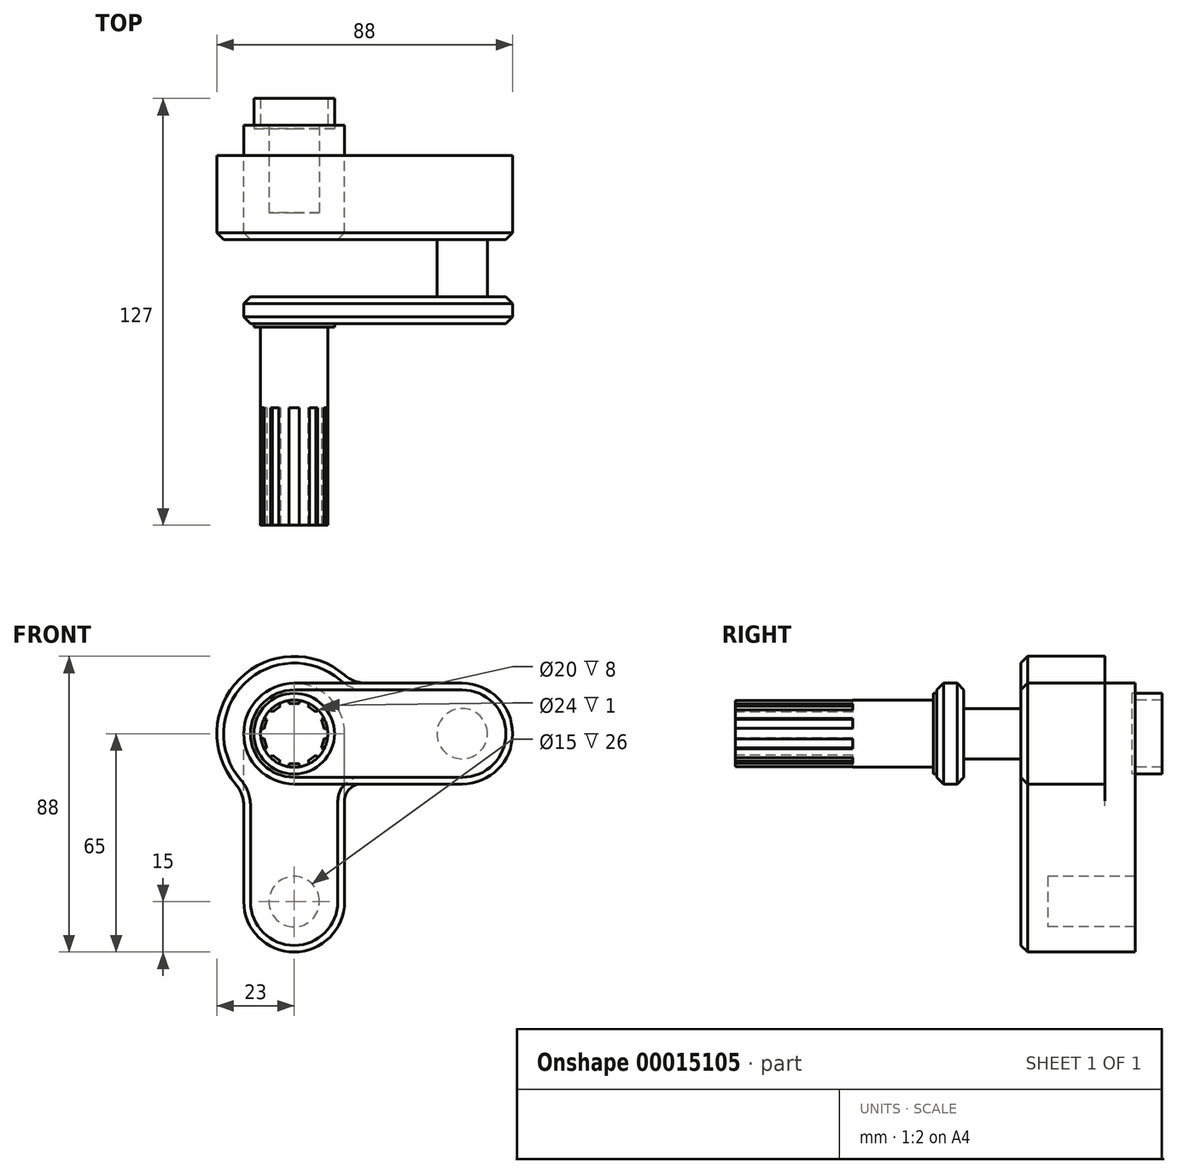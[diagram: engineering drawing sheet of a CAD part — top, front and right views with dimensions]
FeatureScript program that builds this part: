
annotation { "Feature Type Name" : "Feature", "Feature Type Description" : "" }
export const myFeature = defineFeature(function(context is Context, id is Id, definition is map)
    precondition{}
    {
        {
            var Q0;
            Q0=qCreatedBy(makeId("Front.planeOp"),FACE);
            var sketch = newSketch(context, id + "F0", { "sketchPlane" : qUnion([Q0])});
            skArc(sketch, "E0", {"start": v(15.01, 17.42) * mm, "mid": v(-16.26, 16.26) * mm, "end": v(-17.42, -15.01) * mm});
            skLineSegment(sketch, "E1", {"start": v(0, 0) * mm, "end": v(77.35, 0) * mm, "construction": true});
            skLineSegment(sketch, "E2", {"start": v(0, 0) * mm, "end": v(0, -78.85) * mm, "construction": true});
            skArc(sketch, "E3", {"start": v(50, -15) * mm, "mid": v(65, 0) * mm, "end": v(50, 15) * mm});
            skArc(sketch, "E4", {"start": v(-15, -50) * mm, "mid": v(0, -65) * mm, "end": v(15, -50) * mm});
            skLineSegment(sketch, "E5", {"start": v(50, 15) * mm, "end": v(0, 15) * mm});
            skLineSegment(sketch, "E6", {"start": v(50, -15) * mm, "end": v(0, -15) * mm});
            skLineSegment(sketch, "E7", {"start": v(-15, -50) * mm, "end": v(-15, 0) * mm});
            skLineSegment(sketch, "E8", {"start": v(15, -50) * mm, "end": v(15, 0) * mm});
            skPoint(sketch, "E9.visualSharp", {"position": v(15, -15) * mm});
            skArc(sketch, "E9.filletArc", {"start": v(20, -15) * mm, "mid": v(16.46, -16.46) * mm, "end": v(15, -20) * mm});
            skPoint(sketch, "E10.visualSharp", {"position": v(-15, -17.44) * mm});
            skArc(sketch, "E10.filletArc", {"start": v(-15, -21.54) * mm, "mid": v(-15.63, -18.06) * mm, "end": v(-17.42, -15.01) * mm});
            skPoint(sketch, "E11.visualSharp", {"position": v(17.44, 15) * mm});
            skArc(sketch, "E11.filletArc", {"start": v(15.01, 17.42) * mm, "mid": v(18.06, 15.63) * mm, "end": v(21.54, 15) * mm});
            skCircle(sketch, "E12", {"center": v(0, 0) * mm, "radius": 10 * mm});
            skCircle(sketch, "E13", {"center": v(0, 0) * mm, "radius": 12 * mm});
            skCircle(sketch, "E14", {"center": v(50, 0) * mm, "radius": 7.5 * mm});
            skCircle(sketch, "E15", {"center": v(0, -50) * mm, "radius": 7.5 * mm});
            skCircle(sketch, "E16", {"center": v(0, 0) * mm, "radius": 15 * mm});
            skSolve(sketch);
        }
        {
            var Q0;
            Q0=makeQuery(id+"F0.imprint","IMPRINT",FACE,{"disambiguationData":[TD([[makeQuery(id+"F0.imprint","IMPRINT",EDGE,{"derivedFrom":sQuery(id+"F0.wireOp",EDGE,"E0")}),1.0]])]});
            var Q1;
            {var subQ4=sQuery(id+"F0.wireOp",EDGE,"E4");Q1=makeQuery(id+"F0.imprint","IMPRINT",FACE,{"disambiguationData":[TD([[makeQuery(id+"F0.imprint","IMPRINT",EDGE,{"derivedFrom":subQ4}),1.0]])]});}
            var Q2;
            {var subQ0=sQuery(id+"F0.wireOp",EDGE,"E9.filletArc");Q2=makeQuery(id+"F0.imprint","IMPRINT",FACE,{"disambiguationData":[TD([[makeQuery(id+"F0.imprint","IMPRINT",EDGE,{"derivedFrom":subQ0}),-1.0]])]});}
            var Q3;
            {var subQ8=sQuery(id+"F0.wireOp",EDGE,"E3");Q3=makeQuery(id+"F0.imprint","IMPRINT",FACE,{"disambiguationData":[TD([[makeQuery(id+"F0.imprint","IMPRINT",EDGE,{"derivedFrom":subQ8}),1.0]])]});}
            var Q4;
            Q4=makeQuery(id+"F0.imprint","IMPRINT",FACE,{"disambiguationData":[TD([[makeQuery(id+"F0.imprint","IMPRINT",EDGE,{"derivedFrom":sQuery(id+"F0.wireOp",EDGE,"E13")}),-1.0]])]});
            var Q5;
            Q5=makeQuery(id+"F0.imprint","IMPRINT",FACE,{"disambiguationData":[TD([[makeQuery(id+"F0.imprint","IMPRINT",EDGE,{"derivedFrom":sQuery(id+"F0.wireOp",EDGE,"E12")}),-1.0]])]});
            var Q6;
            Q6=makeQuery(id+"F0.imprint","IMPRINT",FACE,{"disambiguationData":[TD([[makeQuery(id+"F0.imprint","IMPRINT",EDGE,{"derivedFrom":sQuery(id+"F0.wireOp",EDGE,"E12")}),1.0]])]});
            var Q7;
            {var subQ0=sQuery(id+"F0.wireOp",EDGE,"E16");var subQ3=sQuery(id+"F0.wireOp",EDGE,"E6");var subQ4=makeQuery(id+"F0.imprint","INTERSECT",VERTEX,{"derivedFrom":[subQ3,subQ0]});Q7=makeQuery(id+"F0.imprint","IMPRINT",FACE,{"disambiguationData":[TD([[makeQuery(id+"F0.imprint","IMPRINT",EDGE,{"disambiguationData":[TD([[subQ4,1.0]])],"derivedFrom":subQ3}),-1.0]])]});}
            var Q8;
            Q8=makeQuery(id+"F0.imprint","IMPRINT",FACE,{"disambiguationData":[TD([[makeQuery(id+"F0.imprint","IMPRINT",EDGE,{"derivedFrom":sQuery(id+"F0.wireOp",EDGE,"E14")}),1.0]])]});
            var Q9;
            Q9=makeQuery(id+"F0.imprint","IMPRINT",FACE,{"disambiguationData":[TD([[makeQuery(id+"F0.imprint","IMPRINT",EDGE,{"derivedFrom":sQuery(id+"F0.wireOp",EDGE,"E15")}),1.0]])]});
            extrude(context, id + "F1", {"entities" : qUnion([Q0, Q1, Q2, Q3, Q4, Q5, Q6, Q7, Q8, Q9]), "endBound" : BoundingType.SYMMETRIC, "depth" : 8 * mm});
        }
        {
            var Q0;
            Q0=makeQuery(id+"F1.opExtrude","CAP_FACE",FACE,{"disambiguationData":[OSD([sQuery(id+"F0.wireOp",EDGE,"E0"),sQuery(id+"F0.wireOp",EDGE,"E3"),sQuery(id+"F0.wireOp",EDGE,"E4"),sQuery(id+"F0.wireOp",EDGE,"E5"),sQuery(id+"F0.wireOp",EDGE,"E6"),sQuery(id+"F0.wireOp",EDGE,"E7"),sQuery(id+"F0.wireOp",EDGE,"E8"),sQuery(id+"F0.wireOp",EDGE,"E9.filletArc"),sQuery(id+"F0.wireOp",EDGE,"E10.filletArc"),sQuery(id+"F0.wireOp",EDGE,"E11.filletArc")])],"isStart":false});
            var sketch = newSketch(context, id + "F2", { "sketchPlane" : qUnion([Q0])});
            skCircle(sketch, "E17.0", {"center": v(50, 0) * mm, "radius": 7.5 * mm});
            skSolve(sketch);
        }
        {
            var Q0;
            Q0=makeQuery(id+"F2.imprint","IMPRINT",FACE,{"disambiguationData":[TD([[makeQuery(id+"F2.imprint","IMPRINT",EDGE,{"derivedFrom":sQuery(id+"F2.wireOp",EDGE,"E17.0")}),1.0]])]});
            extrude(context, id + "F3", {"entities" : qUnion([Q0]), "operationType" : NewBodyOperationType.ADD, "depth" : 17 * mm});
        }
        {
            var Q0;
            Q0=makeQuery(id+"F3.opExtrude","CAP_FACE",FACE,{"disambiguationData":[OSD([sQuery(id+"F2.wireOp",EDGE,"E17.0")])],"isStart":false});
            var sketch = newSketch(context, id + "F4", { "sketchPlane" : qUnion([Q0])});
            skArc(sketch, "E18.0", {"start": v(50, -15) * mm, "mid": v(65, 0) * mm, "end": v(50, 15) * mm});
            skLineSegment(sketch, "E18.1", {"start": v(50, 15) * mm, "end": v(0, 15) * mm});
            skLineSegment(sketch, "E18.2", {"start": v(50, -15) * mm, "end": v(0, -15) * mm});
            skArc(sketch, "E18.3", {"start": v(0, 15) * mm, "mid": v(-15, 0) * mm, "end": v(0, -15) * mm});
            skSolve(sketch);
        }
        {
            var Q0;
            Q0=makeQuery(id+"F4.imprint","IMPRINT",FACE,{"disambiguationData":[TD([[makeQuery(id+"F4.imprint","IMPRINT",EDGE,{"derivedFrom":sQuery(id+"F4.wireOp",EDGE,"E18.0")}),1.0]])]});
            var Q1;
            Q1=makeQuery(id+"F4.imprint","IMPRINT",FACE,{"disambiguationData":[TD([[makeQuery(id+"F4.imprint","IMPRINT",EDGE,{"derivedFrom":makeQuery(id+"F3.opExtrude","CAP_EDGE",EDGE,{"disambiguationData":[OSD([sQuery(id+"F2.wireOp",EDGE,"E17.0")])],"isStart":false})}),1.0]])]});
            extrude(context, id + "F5", {"entities" : qUnion([Q0, Q1]), "operationType" : NewBodyOperationType.ADD, "depth" : 8 * mm});
        }
        {
            var Q0;
            Q0=makeQuery(id+"F5.opExtrude","CAP_FACE",FACE,{"disambiguationData":[OSD([sQuery(id+"F4.wireOp",EDGE,"E18.0"),sQuery(id+"F4.wireOp",EDGE,"E18.1"),sQuery(id+"F4.wireOp",EDGE,"E18.2"),sQuery(id+"F4.wireOp",EDGE,"E18.3")])],"isStart":false});
            var sketch = newSketch(context, id + "F6", { "sketchPlane" : qUnion([Q0])});
            skCircle(sketch, "E19.0", {"center": v(0, 0) * mm, "radius": 12 * mm});
            skSolve(sketch);
        }
        {
            var Q0;
            Q0=makeQuery(id+"F6.imprint","IMPRINT",FACE,{"disambiguationData":[TD([[makeQuery(id+"F6.imprint","IMPRINT",EDGE,{"derivedFrom":sQuery(id+"F6.wireOp",EDGE,"E19.0")}),1.0]])]});
            extrude(context, id + "F7", {"entities" : qUnion([Q0]), "operationType" : NewBodyOperationType.ADD, "depth" : 1 * mm});
        }
        {
            var Q0;
            Q0=makeQuery(id+"F7.opExtrude","CAP_FACE",FACE,{"disambiguationData":[OSD([sQuery(id+"F6.wireOp",EDGE,"E19.0")])],"isStart":false});
            var sketch = newSketch(context, id + "F8", { "sketchPlane" : qUnion([Q0])});
            skCircle(sketch, "E20.0", {"center": v(0, 0) * mm, "radius": 10 * mm});
            skSolve(sketch);
        }
        {
            var Q0;
            Q0=makeQuery(id+"F8.imprint","IMPRINT",FACE,{"disambiguationData":[TD([[makeQuery(id+"F8.imprint","IMPRINT",EDGE,{"derivedFrom":sQuery(id+"F8.wireOp",EDGE,"E20.0")}),1.0]])]});
            extrude(context, id + "F9", {"entities" : qUnion([Q0]), "operationType" : NewBodyOperationType.ADD, "depth" : 59 * mm});
        }
        {
            var Q0;
            Q0=makeQuery(id+"F1.opExtrude","CAP_FACE",FACE,{"disambiguationData":[OSD([sQuery(id+"F0.wireOp",EDGE,"E0"),sQuery(id+"F0.wireOp",EDGE,"E3"),sQuery(id+"F0.wireOp",EDGE,"E4"),sQuery(id+"F0.wireOp",EDGE,"E5"),sQuery(id+"F0.wireOp",EDGE,"E6"),sQuery(id+"F0.wireOp",EDGE,"E7"),sQuery(id+"F0.wireOp",EDGE,"E8"),sQuery(id+"F0.wireOp",EDGE,"E9.filletArc"),sQuery(id+"F0.wireOp",EDGE,"E10.filletArc"),sQuery(id+"F0.wireOp",EDGE,"E11.filletArc")])],"isStart":true});
            var sketch = newSketch(context, id + "F10", { "sketchPlane" : qUnion([Q0])});
            skCircle(sketch, "E21.0", {"center": v(0, -50) * mm, "radius": 7.5 * mm});
            skSolve(sketch);
        }
        {
            var Q0;
            Q0=makeQuery(id+"F10.imprint","IMPRINT",FACE,{"disambiguationData":[TD([[makeQuery(id+"F10.imprint","IMPRINT",EDGE,{"derivedFrom":sQuery(id+"F10.wireOp",EDGE,"E21.0")}),-1.0]])]});
            extrude(context, id + "F11", {"entities" : qUnion([Q0]), "operationType" : NewBodyOperationType.ADD, "depth" : 17 * mm});
        }
        {
            var Q0;
            Q0=makeQuery(id+"F11.opExtrude","CAP_FACE",FACE,{"disambiguationData":[OSD([sQuery(id+"F10.wireOp",EDGE,"E21.0")])],"isStart":false});
            var sketch = newSketch(context, id + "F12", { "sketchPlane" : qUnion([Q0])});
            skArc(sketch, "E22.0", {"start": v(15, -50) * mm, "mid": v(0, -65) * mm, "end": v(-15, -50) * mm});
            skLineSegment(sketch, "E23.0", {"start": v(-15, -50) * mm, "end": v(-15, 0) * mm});
            skLineSegment(sketch, "E24.0", {"start": v(15, -50) * mm, "end": v(15, 0) * mm});
            skArc(sketch, "E25.0", {"start": v(-15, 0) * mm, "mid": v(0, 15) * mm, "end": v(15, 0) * mm});
            skSolve(sketch);
        }
        {
            var Q0;
            Q0=makeQuery(id+"F12.imprint","IMPRINT",FACE,{"disambiguationData":[TD([[makeQuery(id+"F12.imprint","IMPRINT",EDGE,{"derivedFrom":sQuery(id+"F12.wireOp",EDGE,"E22.0")}),-1.0]])]});
            var Q1;
            Q1=makeQuery(id+"F12.imprint","IMPRINT",FACE,{"disambiguationData":[TD([[makeQuery(id+"F12.imprint","IMPRINT",EDGE,{"derivedFrom":makeQuery(id+"F11.opExtrude","CAP_EDGE",EDGE,{"disambiguationData":[OSD([sQuery(id+"F10.wireOp",EDGE,"E21.0")])],"isStart":false})}),-1.0]])]});
            extrude(context, id + "F13", {"entities" : qUnion([Q0, Q1]), "operationType" : NewBodyOperationType.ADD, "depth" : 8 * mm});
        }
        {
            var Q0;
            Q0=makeQuery(id+"F13.opExtrude","CAP_FACE",FACE,{"disambiguationData":[OSD([sQuery(id+"F12.wireOp",EDGE,"E22.0"),sQuery(id+"F12.wireOp",EDGE,"E23.0"),sQuery(id+"F12.wireOp",EDGE,"E24.0"),sQuery(id+"F12.wireOp",EDGE,"E25.0")])],"isStart":false});
            var sketch = newSketch(context, id + "F14", { "sketchPlane" : qUnion([Q0])});
            skCircle(sketch, "E26.0", {"center": v(0, 0) * mm, "radius": 12 * mm});
            skSolve(sketch);
        }
        {
            var Q0;
            Q0=makeQuery(id+"F14.imprint","IMPRINT",FACE,{"disambiguationData":[TD([[makeQuery(id+"F14.imprint","IMPRINT",EDGE,{"derivedFrom":sQuery(id+"F14.wireOp",EDGE,"E26.0")}),-1.0]])]});
            extrude(context, id + "F15", {"entities" : qUnion([Q0]), "operationType" : NewBodyOperationType.ADD, "depth" : 1 * mm});
        }
        {
            var Q0;
            Q0=makeQuery(id+"F15.opExtrude","CAP_FACE",FACE,{"disambiguationData":[OSD([sQuery(id+"F14.wireOp",EDGE,"E26.0")])],"isStart":false});
            var sketch = newSketch(context, id + "F16", { "sketchPlane" : qUnion([Q0])});
            skCircle(sketch, "E27.0", {"center": v(0, 0) * mm, "radius": 10 * mm});
            skSolve(sketch);
        }
        {
            var Q0;
            Q0=makeQuery(id+"F16.imprint","IMPRINT",FACE,{"disambiguationData":[TD([[makeQuery(id+"F16.imprint","IMPRINT",EDGE,{"derivedFrom":sQuery(id+"F16.wireOp",EDGE,"E27.0")}),-1.0]])]});
            extrude(context, id + "F17", {"entities" : qUnion([Q0]), "operationType" : NewBodyOperationType.ADD, "depth" : 8 * mm});
        }
        {
            var Q0;
            Q0=makeQuery(id+"F9.opExtrude","CAP_FACE",FACE,{"disambiguationData":[OSD([sQuery(id+"F8.wireOp",EDGE,"E20.0")])],"isStart":false});
            var sketch = newSketch(context, id + "F18", { "sketchPlane" : qUnion([Q0])});
            skCircle(sketch, "E28.0", {"center": v(0, 0) * mm, "radius": 10 * mm, "construction": true});
            skLineSegment(sketch, "E29", {"start": v(0, 0) * mm, "end": v(0, 10) * mm, "construction": true});
            skLineSegment(sketch, "E30.rect.bottom", {"start": v(1.5, 9) * mm, "end": v(-1.5, 9) * mm});
            skLineSegment(sketch, "E30.rect.top", {"start": v(1.5, 11) * mm, "end": v(-1.5, 11) * mm});
            skLineSegment(sketch, "E30.rect.left", {"start": v(1.5, 9) * mm, "end": v(1.5, 11) * mm});
            skLineSegment(sketch, "E30.rect.right", {"start": v(-1.5, 9) * mm, "end": v(-1.5, 11) * mm});
            skPoint(sketch, "E30.rect.middle", {"position": v(0, 10) * mm});
            skSolve(sketch);
        }
        {
            var Q0;
            {var subQ5=sQuery(id+"F18.wireOp",EDGE,"E30.rect.bottom");Q0=makeQuery(id+"F18.imprint","IMPRINT",FACE,{"disambiguationData":[TD([[makeQuery(id+"F18.imprint","IMPRINT",EDGE,{"derivedFrom":subQ5}),-1.0]])]});}
            var Q1;
            {var subQ5=sQuery(id+"F18.wireOp",EDGE,"E30.rect.top");Q1=makeQuery(id+"F18.imprint","IMPRINT",FACE,{"disambiguationData":[TD([[makeQuery(id+"F18.imprint","IMPRINT",EDGE,{"derivedFrom":subQ5}),1.0]])]});}
            extrude(context, id + "F19", {"entities" : qUnion([Q0, Q1]), "operationType" : NewBodyOperationType.REMOVE, "oppositeDirection" : true, "depth" : 35 * mm});
        }
        {
            var Q0;
            Q0=makeQuery(id+"F19.boolean.opBoolean","COPY",FACE,{"derivedFrom":makeQuery(id+"F19.opExtrude","SWEPT_FACE",FACE,{"disambiguationData":[OSD([sQuery(id+"F18.wireOp",EDGE,"E30.rect.right")])]})});
            var Q1;
            Q1=makeQuery(id+"F19.boolean.opBoolean","COPY",FACE,{"derivedFrom":makeQuery(id+"F19.opExtrude","SWEPT_FACE",FACE,{"disambiguationData":[OSD([sQuery(id+"F18.wireOp",EDGE,"E30.rect.bottom")])]})});
            var Q2;
            Q2=makeQuery(id+"F19.boolean.opBoolean","COPY",FACE,{"derivedFrom":makeQuery(id+"F19.opExtrude","CAP_FACE",FACE,{"disambiguationData":[OSD([sQuery(id+"F18.wireOp",EDGE,"E30.rect.bottom"),sQuery(id+"F18.wireOp",EDGE,"E30.rect.top"),sQuery(id+"F18.wireOp",EDGE,"E30.rect.left"),sQuery(id+"F18.wireOp",EDGE,"E30.rect.right")])],"isStart":false})});
            var Q3;
            Q3=makeQuery(id+"F19.boolean.opBoolean","COPY",FACE,{"derivedFrom":makeQuery(id+"F19.opExtrude","SWEPT_FACE",FACE,{"disambiguationData":[OSD([sQuery(id+"F18.wireOp",EDGE,"E30.rect.left")])]})});
            var Q4;
            Q4=makeQuery(id+"F9.opExtrude","SWEPT_FACE",FACE,{"disambiguationData":[OSD([sQuery(id+"F8.wireOp",EDGE,"E20.0")])]});
            circularPattern(context, id + "F20", {"faces" : qUnion([Q0, Q1, Q2, Q3]), "axis" : qUnion([Q4]), "angle" : 360 * degree, "instanceCount" : round(10), "equalSpace" : true, "patternType" : PatternType.FACE});
        }
        {
            var Q0;
            Q0=makeQuery(id+"F5.opExtrude","CAP_EDGE",EDGE,{"disambiguationData":[OSD([sQuery(id+"F4.wireOp",EDGE,"E18.1")])],"isStart":false});
            var Q1;
            Q1=makeQuery(id+"F5.opExtrude","CAP_EDGE",EDGE,{"disambiguationData":[OSD([sQuery(id+"F4.wireOp",EDGE,"E18.1")])],"isStart":true});
            var Q2;
            Q2=makeQuery(id+"F1.opExtrude","CAP_EDGE",EDGE,{"disambiguationData":[OSD([sQuery(id+"F0.wireOp",EDGE,"E8")])],"isStart":false});
            var Q3;
            Q3=makeQuery(id+"F1.opExtrude","CAP_EDGE",EDGE,{"disambiguationData":[OSD([sQuery(id+"F0.wireOp",EDGE,"E8")])],"isStart":true});
            var Q4;
            Q4=makeQuery(id+"F13.opExtrude","CAP_EDGE",EDGE,{"disambiguationData":[OSD([sQuery(id+"F12.wireOp",EDGE,"E23.0")])],"isStart":true});
            var Q5;
            Q5=makeQuery(id+"F13.opExtrude","CAP_EDGE",EDGE,{"disambiguationData":[OSD([sQuery(id+"F12.wireOp",EDGE,"E23.0")])],"isStart":false});
            chamfer(context, id + "F21", {"entities" : qUnion([Q0, Q1, Q2, Q3, Q4, Q5]), "width" : 2 * mm, "tangentPropagation" : true});
        }
    });
